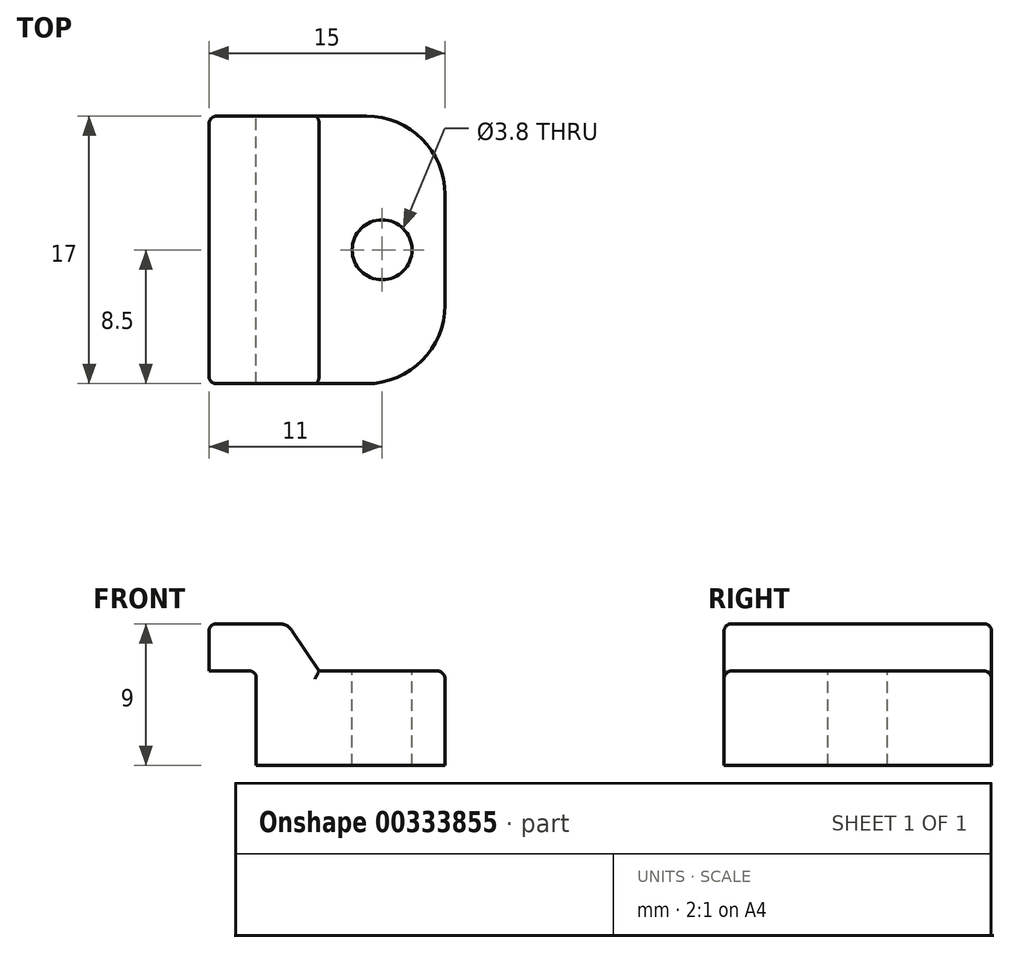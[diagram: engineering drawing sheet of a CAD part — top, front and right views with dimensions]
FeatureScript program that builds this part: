
annotation { "Feature Type Name" : "Feature", "Feature Type Description" : "" }
export const myFeature = defineFeature(function(context is Context, id is Id, definition is map)
    precondition{}
    {
        {
            var Q0;
            Q0=qCreatedBy(makeId("Front.planeOp"),FACE);
            var sketch = newSketch(context, id + "F0", { "sketchPlane" : qUnion([Q0])});
            skLineSegment(sketch, "E0", {"start": v(0, 0) * mm, "end": v(0, 5.59) * mm});
            skLineSegment(sketch, "E1", {"start": v(0.41, 6) * mm, "end": v(3, 6) * mm});
            skLineSegment(sketch, "E2", {"start": v(3, 6) * mm, "end": v(3, 9) * mm});
            skLineSegment(sketch, "E3", {"start": v(0, 0) * mm, "end": v(-12, 0) * mm});
            skLineSegment(sketch, "E4", {"start": v(-12, 0) * mm, "end": v(-12, 6) * mm});
            skLineSegment(sketch, "E5", {"start": v(-12, 6) * mm, "end": v(-2.83, 6) * mm});
            skLineSegment(sketch, "E6", {"start": v(3, 9) * mm, "end": v(-2, 9) * mm});
            skPoint(sketch, "E7.visualSharp", {"position": v(-4, 6) * mm});
            skPoint(sketch, "E8.visualSharp", {"position": v(1, 9) * mm});
            skPoint(sketch, "E9.visualSharp", {"position": v(0, 6) * mm});
            skArc(sketch, "E9.filletArc", {"start": v(0.41, 6) * mm, "mid": v(0.12, 5.88) * mm, "end": v(0, 5.59) * mm});
            skLineSegment(sketch, "E10", {"start": v(-4, 6) * mm, "end": v(-2.83, 6) * mm});
            skLineSegment(sketch, "E11", {"start": v(-2, 9) * mm, "end": v(-4, 6) * mm});
            skSolve(sketch);
        }
        {
            var Q0;
            Q0=qSketchRegion(id+"F0",true);
            extrude(context, id + "F1", {"entities" : qUnion([Q0]), "depth" : 17 * mm});
        }
        {
            var Q0;
            Q0=makeQuery(id+"F1.opExtrude","SWEPT_EDGE",EDGE,{"disambiguationData":[OSD([sQuery(id+"F0.wireOp",EDGE,"E2"),sQuery(id+"F0.wireOp",EDGE,"E6")])]});
            fillet(context, id + "F2", {"entities" : qUnion([Q0]), "radius" : 0.5 * mm, "tangentPropagation" : true, "allowEdgeOverflow" : false});
        }
        {
            var Q0;
            Q0=makeQuery(id+"F1.opExtrude","SWEPT_FACE",FACE,{"disambiguationData":[OSD([sQuery(id+"F0.wireOp",EDGE,"E5")])]});
            var sketch = newSketch(context, id + "F3", { "sketchPlane" : qUnion([Q0])});
            skCircle(sketch, "E12", {"center": v(-8, -8.5) * mm, "radius": 1.9 * mm});
            skPoint(sketch, "E12.centerSnap0", {"position": v(-8, -17) * mm});
            skPoint(sketch, "E12.centerSnap1", {"position": v(-12, -8.5) * mm});
            skSolve(sketch);
        }
        {
            var Q0;
            Q0=qSketchRegion(id+"F3",true);
            extrude(context, id + "F4", {"entities" : qUnion([Q0]), "operationType" : NewBodyOperationType.REMOVE, "oppositeDirection" : true, "depth" : 25 * mm});
        }
        {
            var Q0;
            Q0=makeQuery(id+"F1.opExtrude","CAP_EDGE",EDGE,{"disambiguationData":[OSD([sQuery(id+"F0.wireOp",EDGE,"E4")])],"isStart":false});
            var Q1;
            Q1=makeQuery(id+"F1.opExtrude","CAP_EDGE",EDGE,{"disambiguationData":[OSD([sQuery(id+"F0.wireOp",EDGE,"E4")])],"isStart":true});
            fillet(context, id + "F5", {"entities" : qUnion([Q0, Q1]), "radius" : 5 * mm, "tangentPropagation" : true, "allowEdgeOverflow" : false});
        }
        {
            var Q0;
            Q0=makeQuery(id+"F5.opFillet","BLEND_EDGE",EDGE,{"blendedFrom":[makeQuery(id+"F1.opExtrude","CAP_EDGE",EDGE,{"disambiguationData":[OSD([sQuery(id+"F0.wireOp",EDGE,"E4")])],"isStart":false}),makeQuery(id+"F1.opExtrude","SWEPT_FACE",FACE,{"disambiguationData":[OSD([sQuery(id+"F0.wireOp",EDGE,"E5")])]})],"blendedInto":[makeQuery(id+"F1.opExtrude","SWEPT_FACE",FACE,{"disambiguationData":[OSD([sQuery(id+"F0.wireOp",EDGE,"E5")])]})]});
            fillet(context, id + "F6", {"entities" : qUnion([Q0]), "radius" : 0.5 * mm, "tangentPropagation" : true, "allowEdgeOverflow" : false});
        }
        {
            var Q0;
            Q0=makeQuery(id+"F1.opExtrude","SWEPT_EDGE",EDGE,{"disambiguationData":[OSD([sQuery(id+"F0.wireOp",EDGE,"E6"),sQuery(id+"F0.wireOp",EDGE,"E11")])]});
            fillet(context, id + "F7", {"entities" : qUnion([Q0]), "radius" : 1 * mm, "tangentPropagation" : true, "allowEdgeOverflow" : false});
        }
        {
            var Q0;
            Q0=makeQuery(id+"F1.opExtrude","CAP_EDGE",EDGE,{"disambiguationData":[OSD([sQuery(id+"F0.wireOp",EDGE,"E11")])],"isStart":false});
            var Q1;
            Q1=makeQuery(id+"F1.opExtrude","CAP_EDGE",EDGE,{"disambiguationData":[OSD([sQuery(id+"F0.wireOp",EDGE,"E11")])],"isStart":true});
            fillet(context, id + "F8", {"entities" : qUnion([Q0, Q1]), "radius" : 0.5 * mm, "tangentPropagation" : true, "allowEdgeOverflow" : false});
        }
        {
            var Q0;
            Q0=makeQuery(id+"F1.opExtrude","SWEPT_FACE",FACE,{"disambiguationData":[OSD([sQuery(id+"F0.wireOp",EDGE,"E2")])]});
            cPlane(context, id + "F9", {"entities" : qUnion([Q0]), "cplaneType" : CPlaneType.OFFSET, "offset" : 1 * mm, "width" : 150 * mm, "height" : 150 * mm});
        }
        {
            var Q0;
            Q0=makeQuery(id+"F1.opExtrude","SWEPT_BODY",BODY,{"disambiguationData":[OSD([sQuery(id+"F0.wireOp",EDGE,"E0"),sQuery(id+"F0.wireOp",EDGE,"E1"),sQuery(id+"F0.wireOp",EDGE,"E2"),sQuery(id+"F0.wireOp",EDGE,"E3"),sQuery(id+"F0.wireOp",EDGE,"E4"),sQuery(id+"F0.wireOp",EDGE,"E5"),sQuery(id+"F0.wireOp",EDGE,"E6"),sQuery(id+"F0.wireOp",EDGE,"E9.filletArc"),sQuery(id+"F0.wireOp",EDGE,"E11")])]});
            var Q1;
            Q1=qCreatedBy(id+"F9.planeOp",FACE);
            mirror(context, id + "F10", {"entities" : qUnion([Q0]), "mirrorPlane" : qUnion([Q1])});
        }
        {
            var Q0;
            Q0=makeQuery(id+"F1.opExtrude","SWEPT_BODY",BODY,{"disambiguationData":[OSD([sQuery(id+"F0.wireOp",EDGE,"E0"),sQuery(id+"F0.wireOp",EDGE,"E1"),sQuery(id+"F0.wireOp",EDGE,"E2"),sQuery(id+"F0.wireOp",EDGE,"E3"),sQuery(id+"F0.wireOp",EDGE,"E4"),sQuery(id+"F0.wireOp",EDGE,"E5"),sQuery(id+"F0.wireOp",EDGE,"E6"),sQuery(id+"F0.wireOp",EDGE,"E9.filletArc"),sQuery(id+"F0.wireOp",EDGE,"E11")])]});
            deleteBodies(context, id + "F11", {"entities" : qUnion([Q0])});
        }
    });
